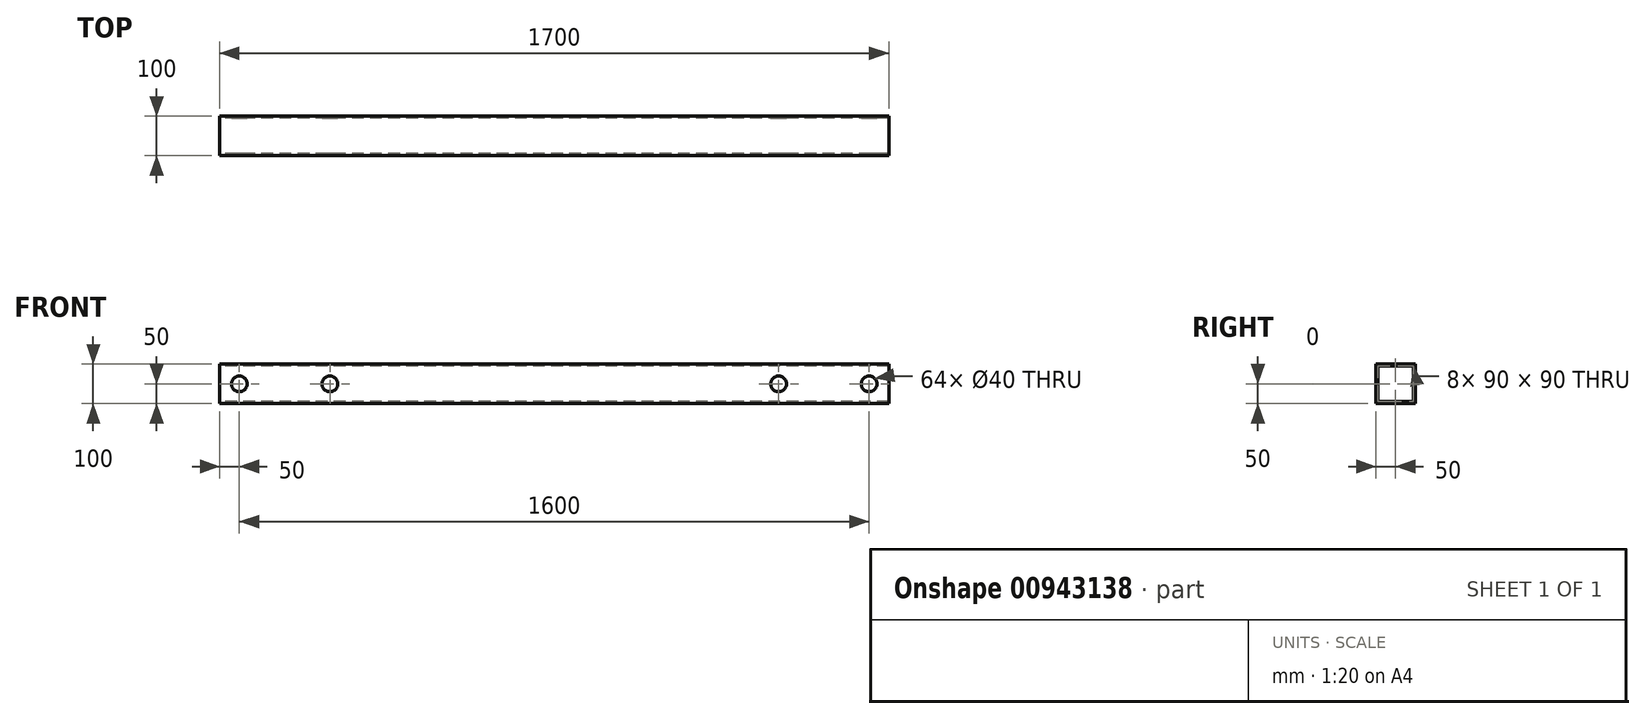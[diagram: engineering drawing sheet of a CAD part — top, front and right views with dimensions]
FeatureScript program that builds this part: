
annotation { "Feature Type Name" : "Feature", "Feature Type Description" : "" }
export const myFeature = defineFeature(function(context is Context, id is Id, definition is map)
    precondition{}
    {
        {
            var Q0;
            Q0=qCreatedBy(makeId("Right.planeOp"),FACE);
            var sketch = newSketch(context, id + "F0", { "sketchPlane" : qUnion([Q0])});
            skLineSegment(sketch, "E0.bottom", {"start": v(50, 50) * mm, "end": v(-50, 50) * mm});
            skLineSegment(sketch, "E0.top", {"start": v(50, -50) * mm, "end": v(-50, -50) * mm});
            skLineSegment(sketch, "E0.left", {"start": v(50, 50) * mm, "end": v(50, -50) * mm});
            skLineSegment(sketch, "E0.right", {"start": v(-50, 50) * mm, "end": v(-50, -50) * mm});
            skPoint(sketch, "E0.middle", {"position": v(0, 0) * mm});
            skLineSegment(sketch, "E1.bottom", {"start": v(-45, -45) * mm, "end": v(45, -45) * mm});
            skLineSegment(sketch, "E1.top", {"start": v(-45, 45) * mm, "end": v(45, 45) * mm});
            skLineSegment(sketch, "E1.left", {"start": v(-45, -45) * mm, "end": v(-45, 45) * mm});
            skLineSegment(sketch, "E1.right", {"start": v(45, -45) * mm, "end": v(45, 45) * mm});
            skSolve(sketch);
        }
        {
            var Q0;
            Q0=qSketchRegion(id+"F0",true);
            extrude(context, id + "F1", {"entities" : qUnion([Q0]), "depth" : 1700 * mm, "offsetDistance" : 25 * mm});
        }
        {
            var Q0;
            Q0=qCreatedBy(makeId("Front.planeOp"),FACE);
            var sketch = newSketch(context, id + "F2", { "sketchPlane" : qUnion([Q0])});
            skCircle(sketch, "E2", {"center": v(50, 0) * mm, "radius": 20 * mm});
            skCircle(sketch, "E3", {"center": v(1650, 0) * mm, "radius": 20 * mm});
            skCircle(sketch, "E4", {"center": v(280, 0) * mm, "radius": 20 * mm});
            skCircle(sketch, "E5", {"center": v(1420, 0) * mm, "radius": 20 * mm});
            skSolve(sketch);
        }
        {
            var Q0;
            Q0 = qSketchRegion(id + "F2", true);
            extrude(context, id + "F3", {"entities" : qUnion([Q0]), "operationType" : NewBodyOperationType.REMOVE, "endBound" : BoundingType.SYMMETRIC, "oppositeDirection" : true, "depth" : 100 * mm, "offsetDistance" : 25 * mm});
        }
    });
